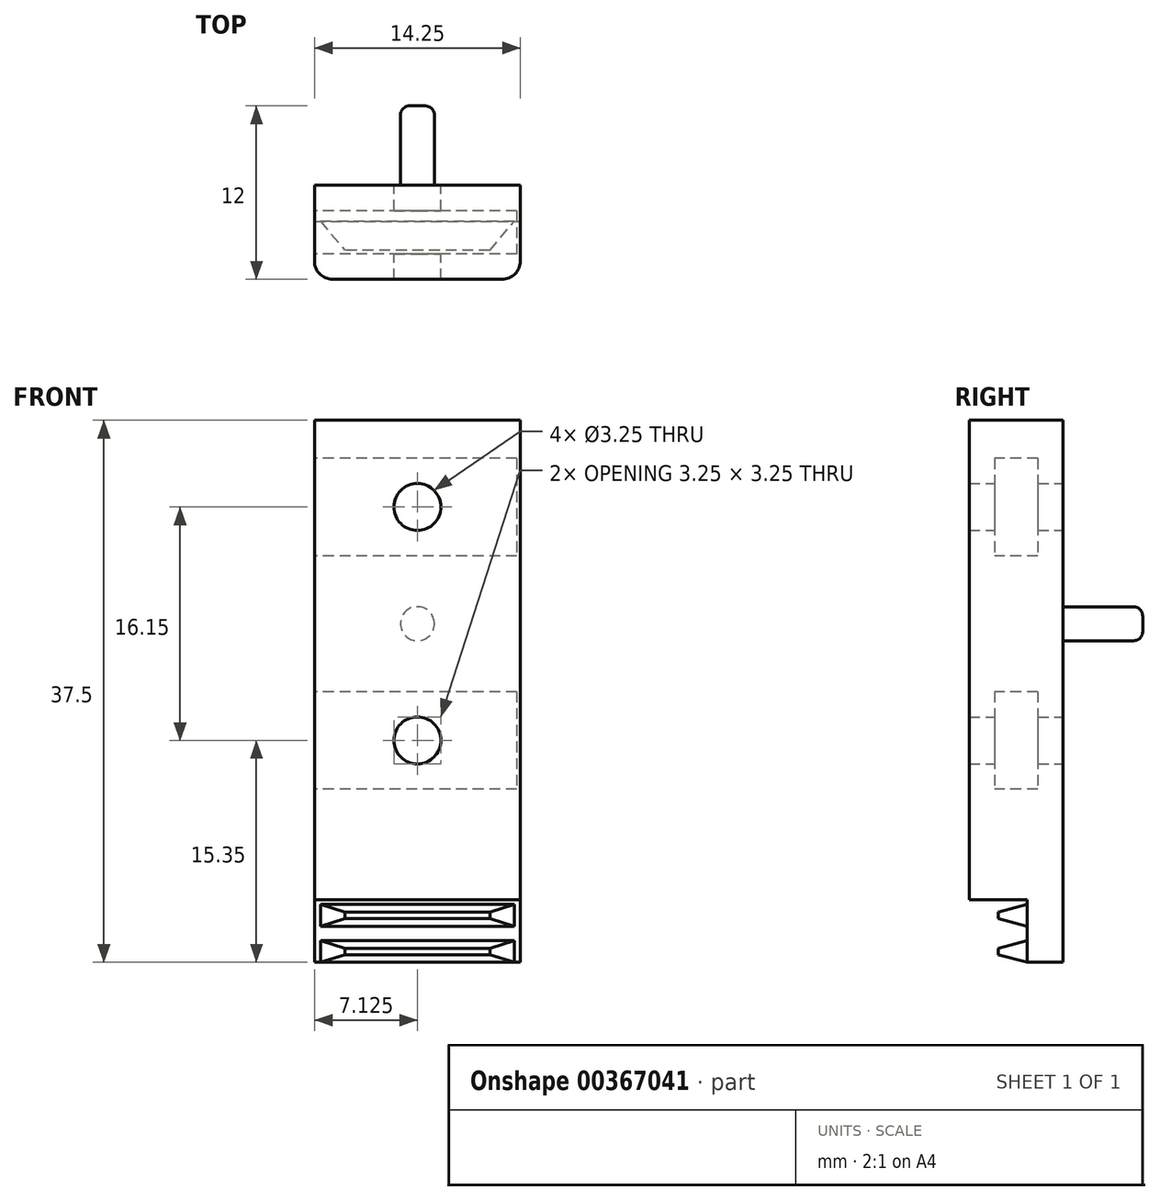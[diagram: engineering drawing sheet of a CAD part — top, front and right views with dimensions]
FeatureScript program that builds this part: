
annotation { "Feature Type Name" : "Feature", "Feature Type Description" : "" }
export const myFeature = defineFeature(function(context is Context, id is Id, definition is map)
    precondition{}
    {
        {
            var Q0;
            Q0=qCreatedBy(makeId("Front.planeOp"),FACE);
            var sketch = newSketch(context, id + "F0", { "sketchPlane" : qUnion([Q0])});
            skLineSegment(sketch, "E0.bottom", {"start": v(0, 0) * mm, "end": v(-14.25, 0) * mm});
            skLineSegment(sketch, "E0.top", {"start": v(0, 37.5) * mm, "end": v(-14.25, 37.5) * mm});
            skLineSegment(sketch, "E0.left", {"start": v(0, 0) * mm, "end": v(0, 37.5) * mm});
            skLineSegment(sketch, "E0.right", {"start": v(-14.25, 0) * mm, "end": v(-14.25, 37.5) * mm});
            skCircle(sketch, "E1", {"center": v(-7.13, 31.5) * mm, "radius": 1.63 * mm});
            skCircle(sketch, "E2", {"center": v(-7.12, 23.43) * mm, "radius": 1.5 * mm});
            skCircle(sketch, "E3", {"center": v(-7.12, 15.35) * mm, "radius": 1.63 * mm});
            skLineSegment(sketch, "E4", {"start": v(-7.12, 37.5) * mm, "end": v(-7.12, 0) * mm, "construction": true});
            skLineSegment(sketch, "E5", {"start": v(-8.75, 31.5) * mm, "end": v(-8.63, 23.43) * mm, "construction": true});
            skLineSegment(sketch, "E6", {"start": v(-8.63, 23.43) * mm, "end": v(-8.75, 15.35) * mm, "construction": true});
            skSolve(sketch);
        }
        {
            var Q0;
            Q0=makeQuery(id+"F0.imprint","IMPRINT",FACE,{"disambiguationData":[TD([[makeQuery(id+"F0.imprint","IMPRINT",EDGE,{"derivedFrom":sQuery(id+"F0.wireOp",EDGE,"E0.bottom")}),-1.0]])]});
            var Q1;
            Q1=makeQuery(id+"F0.imprint","IMPRINT",FACE,{"disambiguationData":[TD([[makeQuery(id+"F0.imprint","IMPRINT",EDGE,{"derivedFrom":sQuery(id+"F0.wireOp",EDGE,"E2")}),1.0]])]});
            extrude(context, id + "F1", {"entities" : qUnion([Q0, Q1]), "depth" : 6.5 * mm});
        }
        {
            var Q0;
            Q0=makeQuery(id+"F1.opExtrude","CAP_FACE",FACE,{"disambiguationData":[OSD([sQuery(id+"F0.wireOp",EDGE,"E0.bottom"),sQuery(id+"F0.wireOp",EDGE,"E0.top"),sQuery(id+"F0.wireOp",EDGE,"E0.left"),sQuery(id+"F0.wireOp",EDGE,"E0.right"),sQuery(id+"F0.wireOp",EDGE,"E1"),sQuery(id+"F0.wireOp",EDGE,"E3")])],"isStart":true});
            var sketch = newSketch(context, id + "F2", { "sketchPlane" : qUnion([Q0])});
            skLineSegment(sketch, "E7", {"start": v(7.13, 31.5) * mm, "end": v(7.12, 15.35) * mm, "construction": true});
            skCircle(sketch, "E8", {"center": v(7.12, 23.43) * mm, "radius": 1.18 * mm});
            skSolve(sketch);
        }
        {
            var Q0;
            Q0 = qSketchRegion(id + "F2", true);
            extrude(context, id + "F3", {"entities" : qUnion([Q0]), "operationType" : NewBodyOperationType.ADD, "depth" : 5.5 * mm});
        }
        {
            var Q0;
            Q0=makeQuery(id+"F3.opExtrude","CAP_EDGE",EDGE,{"disambiguationData":[OSD([sQuery(id+"F2.wireOp",EDGE,"E8")])],"isStart":false});
            fillet(context, id + "F4", {"entities" : qUnion([Q0]), "radius" : 0.64 * mm, "tangentPropagation" : true, "allowEdgeOverflow" : false});
        }
        {
            var Q0;
            Q0=makeQuery(id+"FinUkORYrYptvAC_1.boolean.opBoolean","MERGE",FACE,{"derivedFrom":[makeQuery(id+"F1.opExtrude","SWEPT_FACE",FACE,{"disambiguationData":[OSD([sQuery(id+"F0.wireOp",EDGE,"E0.right")])]}),makeQuery(id+"FinUkORYrYptvAC_1.opExtrude","SWEPT_FACE",FACE,{"disambiguationData":[OSD([sQuery(id+"FCgop3agzBuojqY_1.wireOp",EDGE,"TQxR3b1I-pLeD-3WI0-s3w3-q6DaQqubb28t")])]})]});
            var sketch = newSketch(context, id + "F5", { "sketchPlane" : qUnion([Q0])});
            skLineSegment(sketch, "E9", {"start": v(3.25, 37.5) * mm, "end": v(3.25, 1.27) * mm, "construction": true});
            skLineSegment(sketch, "E10.bottom", {"start": v(1.75, 34.88) * mm, "end": v(4.75, 34.88) * mm});
            skLineSegment(sketch, "E10.top", {"start": v(1.75, 28.12) * mm, "end": v(4.75, 28.12) * mm});
            skLineSegment(sketch, "E10.left", {"start": v(1.75, 34.88) * mm, "end": v(1.75, 28.12) * mm});
            skLineSegment(sketch, "E10.right", {"start": v(4.75, 34.88) * mm, "end": v(4.75, 28.13) * mm});
            skLineSegment(sketch, "E11.bottom", {"start": v(1.75, 18.73) * mm, "end": v(4.75, 18.73) * mm});
            skLineSegment(sketch, "E11.top", {"start": v(1.75, 11.98) * mm, "end": v(4.75, 11.98) * mm});
            skLineSegment(sketch, "E11.left", {"start": v(1.75, 18.73) * mm, "end": v(1.75, 11.98) * mm});
            skLineSegment(sketch, "E11.right", {"start": v(4.75, 18.73) * mm, "end": v(4.75, 11.98) * mm});
            skPoint(sketch, "E12", {"position": v(1.75, 31.5) * mm});
            skPoint(sketch, "E13", {"position": v(1.75, 15.35) * mm});
            skPoint(sketch, "E14", {"position": v(3.25, 18.73) * mm});
            skPoint(sketch, "E15", {"position": v(3.25, 34.88) * mm});
            skSolve(sketch);
        }
        {
            var Q0;
            Q0 = qSketchRegion(id + "F5", true);
            extrude(context, id + "F6", {"entities" : qUnion([Q0]), "operationType" : NewBodyOperationType.REMOVE, "oppositeDirection" : true, "depth" : (14.25 / 2 + 6.88) * mm});
        }
        {
            var Q0;
            Q0=makeQuery(id+"F1.opExtrude","CAP_FACE",FACE,{"disambiguationData":[OSD([sQuery(id+"F0.wireOp",EDGE,"E0.bottom"),sQuery(id+"F0.wireOp",EDGE,"E0.top"),sQuery(id+"F0.wireOp",EDGE,"E0.left"),sQuery(id+"F0.wireOp",EDGE,"E0.right"),sQuery(id+"F0.wireOp",EDGE,"E1"),sQuery(id+"F0.wireOp",EDGE,"E3")])],"isStart":false});
            var sketch = newSketch(context, id + "F7", { "sketchPlane" : qUnion([Q0])});
            skLineSegment(sketch, "E16.bottom", {"start": v(-19.38, 0) * mm, "end": v(5.12, 0) * mm});
            skLineSegment(sketch, "E16.top", {"start": v(-19.37, 4.32) * mm, "end": v(5.12, 4.32) * mm});
            skLineSegment(sketch, "E16.left", {"start": v(-19.38, 0) * mm, "end": v(-19.38, 4.32) * mm});
            skLineSegment(sketch, "E16.right", {"start": v(5.12, 0) * mm, "end": v(5.12, 4.32) * mm});
            skPoint(sketch, "E17", {"position": v(-7.13, 0) * mm});
            skSolve(sketch);
        }
        {
            var Q0;
            Q0 = qSketchRegion(id + "F7", true);
            extrude(context, id + "F8", {"entities" : qUnion([Q0]), "operationType" : NewBodyOperationType.REMOVE, "oppositeDirection" : true, "depth" : 4 * mm});
        }
        {
            var Q0;
            Q0=makeQuery(id+"F8.boolean.opBoolean","COPY",FACE,{"derivedFrom":makeQuery(id+"F8.opExtrude","CAP_FACE",FACE,{"disambiguationData":[OSD([sQuery(id+"F7.wireOp",EDGE,"E16.bottom"),sQuery(id+"F7.wireOp",EDGE,"E16.top"),sQuery(id+"F7.wireOp",EDGE,"E16.left"),sQuery(id+"F7.wireOp",EDGE,"E16.right")])],"isStart":false})});
            var sketch = newSketch(context, id + "F9", { "sketchPlane" : qUnion([Q0])});
            skLineSegment(sketch, "E18", {"start": v(-13.83, 0) * mm, "end": v(-0.43, 0) * mm});
            skLineSegment(sketch, "E19", {"start": v(-0.43, 0) * mm, "end": v(-0.43, 1.5) * mm});
            skLineSegment(sketch, "E20", {"start": v(-0.43, 1.5) * mm, "end": v(-13.83, 1.5) * mm});
            skLineSegment(sketch, "E21", {"start": v(-13.83, 1.5) * mm, "end": v(-13.83, 0) * mm});
            skPoint(sketch, "E22", {"position": v(-7.13, 1.5) * mm});
            skPoint(sketch, "E23", {"position": v(-7.13, 0) * mm});
            skPoint(sketch, "E24.oppositeSnap0", {"position": v(-14.25, 2.16) * mm});
            skLineSegment(sketch, "E24.bottom", {"start": v(-13.83, 4) * mm, "end": v(-0.43, 4) * mm});
            skLineSegment(sketch, "E24.top", {"start": v(-13.83, 2.5) * mm, "end": v(-0.43, 2.5) * mm});
            skLineSegment(sketch, "E24.left", {"start": v(-13.83, 4) * mm, "end": v(-13.83, 2.5) * mm});
            skLineSegment(sketch, "E24.right", {"start": v(-0.43, 4) * mm, "end": v(-0.43, 2.5) * mm});
            skSolve(sketch);
        }
        {
            var Q0;
            Q0 = qSketchRegion(id + "F9", true);
            extrude(context, id + "F10", {"entities" : qUnion([Q0]), "operationType" : NewBodyOperationType.ADD, "depth" : 2 * mm, "hasDraft" : true, "draftAngle" : 15 * degree, "draftPullDirection" : true});
        }
        {
            var Q0;
            Q0=makeQuery(id+"F1.opExtrude","SWEPT_FACE",FACE,{"disambiguationData":[OSD([sQuery(id+"F0.wireOp",EDGE,"E0.bottom")])]});
            var sketch = newSketch(context, id + "F11", { "sketchPlane" : qUnion([Q0])});
            skLineSegment(sketch, "E25", {"start": v(-14.25, 2.5) * mm, "end": v(-13.83, 2.5) * mm});
            skLineSegment(sketch, "E26", {"start": v(-13.83, 2.5) * mm, "end": v(-12.13, 4.51) * mm});
            skLineSegment(sketch, "E27", {"start": v(-12.13, 4.51) * mm, "end": v(-2.13, 4.51) * mm});
            skLineSegment(sketch, "E28", {"start": v(-2.13, 4.51) * mm, "end": v(-0.43, 2.5) * mm});
            skLineSegment(sketch, "E29", {"start": v(-0.43, 2.5) * mm, "end": v(0, 2.5) * mm});
            skLineSegment(sketch, "E30", {"start": v(0, 2.5) * mm, "end": v(0, 4.87) * mm});
            skLineSegment(sketch, "E31", {"start": v(0, 4.87) * mm, "end": v(-14.25, 4.87) * mm});
            skLineSegment(sketch, "E32", {"start": v(-14.25, 4.87) * mm, "end": v(-14.25, 2.5) * mm});
            skPoint(sketch, "E33", {"position": v(-7.13, 4.51) * mm});
            skPoint(sketch, "E34", {"position": v(-7.13, 2.5) * mm});
            skSolve(sketch);
        }
        {
            var Q0;
            Q0 = qSketchRegion(id + "F11", true);
            extrude(context, id + "F12", {"entities" : qUnion([Q0]), "operationType" : NewBodyOperationType.REMOVE, "oppositeDirection" : true, "depth" : 4 * mm});
        }
        {
            var Q0;
            Q0=makeQuery(id+"F8.boolean.opBoolean","COPY",EDGE,{"derivedFrom":makeQuery(id+"F8.opExtrude","CAP_EDGE",EDGE,{"disambiguationData":[OSD([sQuery(id+"F7.wireOp",EDGE,"E16.top")])],"isStart":true})});
            var Q1;
            Q1=makeQuery(id+"F1.opExtrude","CAP_EDGE",EDGE,{"disambiguationData":[OSD([sQuery(id+"F0.wireOp",EDGE,"E0.right")])],"isStart":false});
            var Q2;
            Q2=makeQuery(id+"F1.opExtrude","CAP_EDGE",EDGE,{"disambiguationData":[OSD([sQuery(id+"F0.wireOp",EDGE,"E0.left")])],"isStart":false});
            fillet(context, id + "F13", {"entities" : qUnion([Q0, Q1, Q2]), "radius" : 1.27 * mm, "tangentPropagation" : true, "allowEdgeOverflow" : false});
        }
    });
